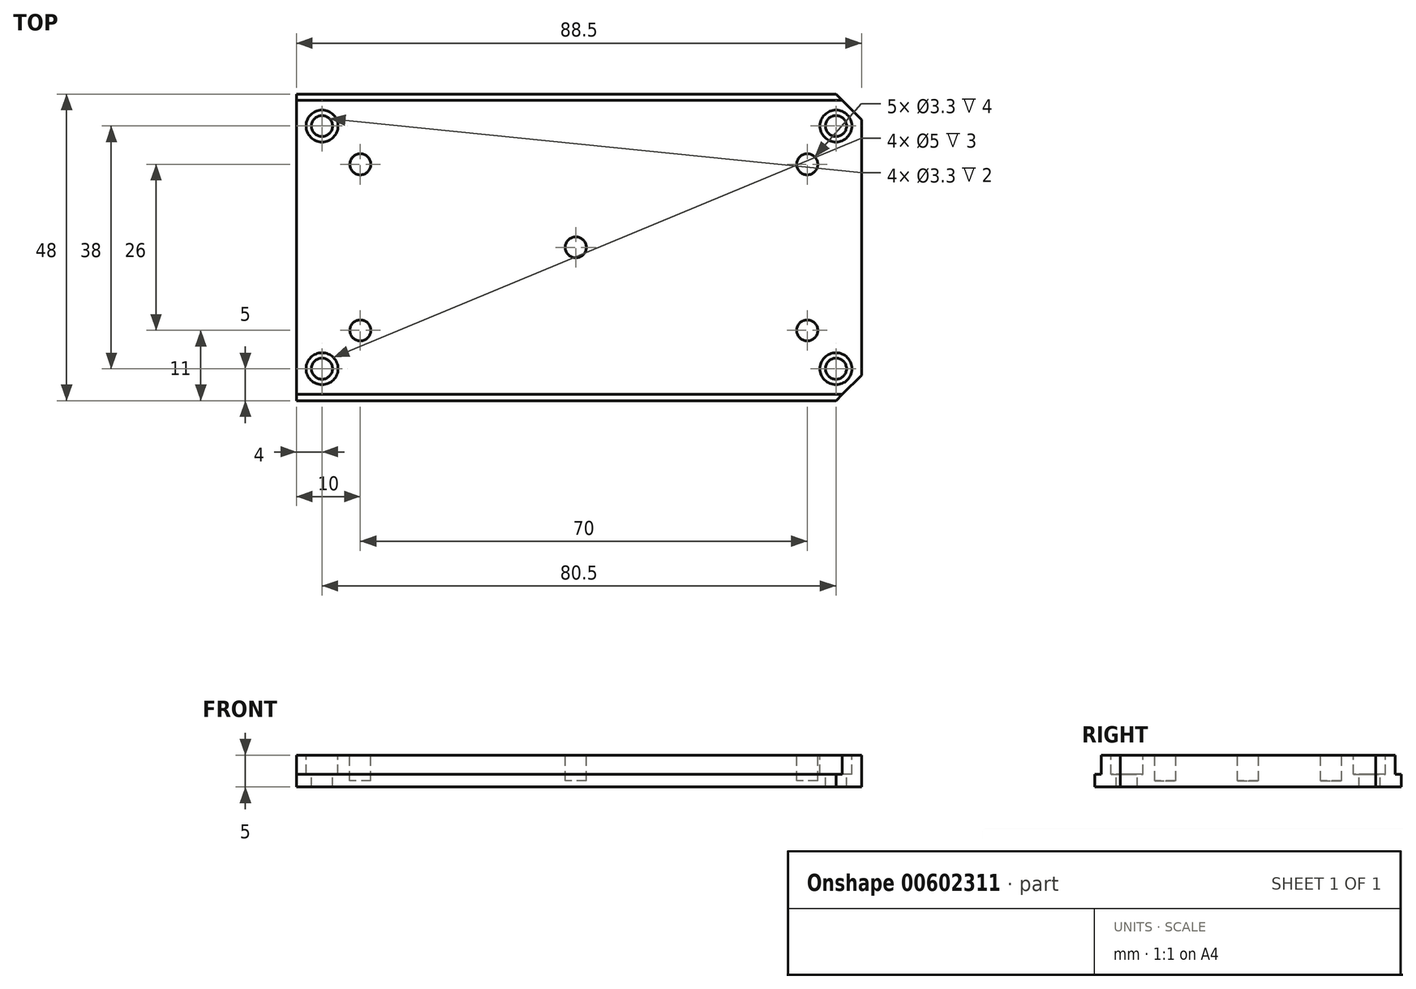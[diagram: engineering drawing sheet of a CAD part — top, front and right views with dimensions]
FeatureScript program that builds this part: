
annotation { "Feature Type Name" : "Feature", "Feature Type Description" : "" }
export const myFeature = defineFeature(function(context is Context, id is Id, definition is map)
    precondition{}
    {
        {
            var Q0;
            Q0=qCreatedBy(makeId("Top.planeOp"),FACE);
            var sketch = newSketch(context, id + "F0", { "sketchPlane" : qUnion([Q0])});
            skLineSegment(sketch, "E0.bottom", {"start": v(0, 0) * mm, "end": v(88.5, 0) * mm});
            skLineSegment(sketch, "E0.top", {"start": v(0, 46) * mm, "end": v(88.5, 46) * mm});
            skLineSegment(sketch, "E0.left", {"start": v(0, 0) * mm, "end": v(0, 46) * mm});
            skLineSegment(sketch, "E0.right", {"start": v(88.5, 0) * mm, "end": v(88.5, 46) * mm});
            skSolve(sketch);
        }
        {
            var Q0;
            Q0=makeQuery(id+"F0.imprint","IMPRINT",FACE,{"disambiguationData":[TD([[makeQuery(id+"F0.imprint","IMPRINT",EDGE,{"derivedFrom":sQuery(id+"F0.wireOp",EDGE,"E0.bottom")}),1.0]])]});
            extrude(context, id + "F1", {"entities" : qUnion([Q0]), "depth" : 5 * mm, "offsetDistance" : 25 * mm});
        }
        {
            var Q0;
            Q0=makeQuery(id+"F1.opExtrude","CAP_FACE",FACE,{"disambiguationData":[OSD([sQuery(id+"F0.wireOp",EDGE,"E0.bottom"),sQuery(id+"F0.wireOp",EDGE,"E0.top"),sQuery(id+"F0.wireOp",EDGE,"E0.left"),sQuery(id+"F0.wireOp",EDGE,"E0.right")])],"isStart":false});
            var sketch = newSketch(context, id + "F2", { "sketchPlane" : qUnion([Q0])});
            skCircle(sketch, "E1", {"center": v(4, 42) * mm, "radius": 2.5 * mm});
            skSolve(sketch);
        }
        {
            var Q0;
            Q0=makeQuery(id+"F2.imprint","IMPRINT",FACE,{"disambiguationData":[TD([[makeQuery(id+"F2.imprint","IMPRINT",EDGE,{"derivedFrom":sQuery(id+"F2.wireOp",EDGE,"E1")}),-1.0]])]});
            var sketch = newSketch(context, id + "F3", { "sketchPlane" : qUnion([Q0])});
            skCircle(sketch, "E2", {"center": v(4, 4) * mm, "radius": 2.5 * mm});
            skSolve(sketch);
        }
        {
            var Q0;
            Q0=makeQuery(id+"F2.imprint","IMPRINT",FACE,{"disambiguationData":[TD([[makeQuery(id+"F2.imprint","IMPRINT",EDGE,{"derivedFrom":sQuery(id+"F2.wireOp",EDGE,"E1")}),-1.0]])]});
            var sketch = newSketch(context, id + "F4", { "sketchPlane" : qUnion([Q0])});
            skCircle(sketch, "E3", {"center": v(84.5, 42) * mm, "radius": 2.5 * mm});
            skSolve(sketch);
        }
        {
            var Q0;
            Q0=makeQuery(id+"F2.imprint","IMPRINT",FACE,{"disambiguationData":[TD([[makeQuery(id+"F2.imprint","IMPRINT",EDGE,{"derivedFrom":sQuery(id+"F2.wireOp",EDGE,"E1")}),-1.0]])]});
            var sketch = newSketch(context, id + "F5", { "sketchPlane" : qUnion([Q0])});
            skCircle(sketch, "E4", {"center": v(84.5, 4) * mm, "radius": 2.5 * mm});
            skSolve(sketch);
        }
        {
            var Q0;
            Q0=makeQuery(id+"F2.imprint","IMPRINT",FACE,{"disambiguationData":[TD([[makeQuery(id+"F2.imprint","IMPRINT",EDGE,{"derivedFrom":sQuery(id+"F2.wireOp",EDGE,"E1")}),1.0]])]});
            extrude(context, id + "F6", {"entities" : qUnion([Q0]), "operationType" : NewBodyOperationType.REMOVE, "oppositeDirection" : true, "depth" : 3 * mm, "offsetDistance" : 25 * mm});
        }
        {
            var Q0;
            Q0=makeQuery(id+"F3.imprint","IMPRINT",FACE,{"disambiguationData":[TD([[makeQuery(id+"F3.imprint","IMPRINT",EDGE,{"derivedFrom":sQuery(id+"F3.wireOp",EDGE,"E2")}),1.0]])]});
            extrude(context, id + "F7", {"entities" : qUnion([Q0]), "operationType" : NewBodyOperationType.REMOVE, "oppositeDirection" : true, "depth" : 3 * mm, "offsetDistance" : 25 * mm});
        }
        {
            var Q0;
            Q0=makeQuery(id+"F4.imprint","IMPRINT",FACE,{"disambiguationData":[TD([[makeQuery(id+"F4.imprint","IMPRINT",EDGE,{"derivedFrom":sQuery(id+"F4.wireOp",EDGE,"E3")}),1.0]])]});
            extrude(context, id + "F8", {"entities" : qUnion([Q0]), "operationType" : NewBodyOperationType.REMOVE, "oppositeDirection" : true, "depth" : 3 * mm, "offsetDistance" : 25 * mm});
        }
        {
            var Q0;
            Q0=makeQuery(id+"F5.imprint","IMPRINT",FACE,{"disambiguationData":[TD([[makeQuery(id+"F5.imprint","IMPRINT",EDGE,{"derivedFrom":sQuery(id+"F5.wireOp",EDGE,"E4")}),1.0]])]});
            extrude(context, id + "F9", {"entities" : qUnion([Q0]), "operationType" : NewBodyOperationType.REMOVE, "oppositeDirection" : true, "depth" : 3 * mm, "offsetDistance" : 25 * mm});
        }
        {
            var Q0;
            Q0=makeQuery(id+"F6.boolean.opBoolean","COPY",FACE,{"derivedFrom":makeQuery(id+"F6.opExtrude","CAP_FACE",FACE,{"disambiguationData":[OSD([sQuery(id+"F2.wireOp",EDGE,"E1")])],"isStart":false})});
            var sketch = newSketch(context, id + "F10", { "sketchPlane" : qUnion([Q0])});
            skCircle(sketch, "E5", {"center": v(4, 42) * mm, "radius": 1.65 * mm});
            skSolve(sketch);
        }
        {
            var Q0;
            Q0=makeQuery(id+"F7.boolean.opBoolean","COPY",FACE,{"derivedFrom":makeQuery(id+"F7.opExtrude","CAP_FACE",FACE,{"disambiguationData":[OSD([sQuery(id+"F3.wireOp",EDGE,"E2")])],"isStart":false})});
            var sketch = newSketch(context, id + "F11", { "sketchPlane" : qUnion([Q0])});
            skCircle(sketch, "E6", {"center": v(4, 4) * mm, "radius": 1.65 * mm});
            skSolve(sketch);
        }
        {
            var Q0;
            Q0=makeQuery(id+"F8.boolean.opBoolean","COPY",FACE,{"derivedFrom":makeQuery(id+"F8.opExtrude","CAP_FACE",FACE,{"disambiguationData":[OSD([sQuery(id+"F4.wireOp",EDGE,"E3")])],"isStart":false})});
            var sketch = newSketch(context, id + "F12", { "sketchPlane" : qUnion([Q0])});
            skCircle(sketch, "E7", {"center": v(84.5, 42) * mm, "radius": 1.65 * mm});
            skSolve(sketch);
        }
        {
            var Q0;
            Q0=makeQuery(id+"F9.boolean.opBoolean","COPY",FACE,{"derivedFrom":makeQuery(id+"F9.opExtrude","CAP_FACE",FACE,{"disambiguationData":[OSD([sQuery(id+"F5.wireOp",EDGE,"E4")])],"isStart":false})});
            var sketch = newSketch(context, id + "F13", { "sketchPlane" : qUnion([Q0])});
            skCircle(sketch, "E8", {"center": v(84.5, 4) * mm, "radius": 1.65 * mm});
            skSolve(sketch);
        }
        {
            var Q0;
            Q0=makeQuery(id+"F12.imprint","IMPRINT",FACE,{"disambiguationData":[TD([[makeQuery(id+"F12.imprint","IMPRINT",EDGE,{"derivedFrom":sQuery(id+"F12.wireOp",EDGE,"E7")}),1.0]])]});
            extrude(context, id + "F14", {"entities" : qUnion([Q0]), "operationType" : NewBodyOperationType.REMOVE, "oppositeDirection" : true, "depth" : 3 * mm, "offsetDistance" : 25 * mm});
        }
        {
            var Q0;
            Q0=makeQuery(id+"F13.imprint","IMPRINT",FACE,{"disambiguationData":[TD([[makeQuery(id+"F13.imprint","IMPRINT",EDGE,{"derivedFrom":sQuery(id+"F13.wireOp",EDGE,"E8")}),1.0]])]});
            extrude(context, id + "F15", {"entities" : qUnion([Q0]), "operationType" : NewBodyOperationType.REMOVE, "oppositeDirection" : true, "depth" : 3 * mm, "offsetDistance" : 25 * mm});
        }
        {
            var Q0;
            Q0=makeQuery(id+"F11.imprint","IMPRINT",FACE,{"disambiguationData":[TD([[makeQuery(id+"F11.imprint","IMPRINT",EDGE,{"derivedFrom":sQuery(id+"F11.wireOp",EDGE,"E6")}),1.0]])]});
            extrude(context, id + "F16", {"entities" : qUnion([Q0]), "operationType" : NewBodyOperationType.REMOVE, "oppositeDirection" : true, "depth" : 3 * mm, "offsetDistance" : 25 * mm});
        }
        {
            var Q0;
            Q0=makeQuery(id+"F10.imprint","IMPRINT",FACE,{"disambiguationData":[TD([[makeQuery(id+"F10.imprint","IMPRINT",EDGE,{"derivedFrom":sQuery(id+"F10.wireOp",EDGE,"E5")}),1.0]])]});
            extrude(context, id + "F17", {"entities" : qUnion([Q0]), "operationType" : NewBodyOperationType.REMOVE, "oppositeDirection" : true, "depth" : 3 * mm, "offsetDistance" : 25 * mm});
        }
        {
            var Q0;
            Q0=makeQuery(id+"F1.opExtrude","CAP_FACE",FACE,{"disambiguationData":[OSD([sQuery(id+"F0.wireOp",EDGE,"E0.bottom"),sQuery(id+"F0.wireOp",EDGE,"E0.top"),sQuery(id+"F0.wireOp",EDGE,"E0.left"),sQuery(id+"F0.wireOp",EDGE,"E0.right")])],"isStart":false});
            var sketch = newSketch(context, id + "F18", { "sketchPlane" : qUnion([Q0])});
            skCircle(sketch, "E9", {"center": v(43.75, 23) * mm, "radius": 1.65 * mm});
            skSolve(sketch);
        }
        {
            var Q0;
            Q0=makeQuery(id+"F18.imprint","IMPRINT",FACE,{"disambiguationData":[TD([[makeQuery(id+"F18.imprint","IMPRINT",EDGE,{"derivedFrom":sQuery(id+"F18.wireOp",EDGE,"E9")}),1.0]])]});
            extrude(context, id + "F19", {"entities" : qUnion([Q0]), "operationType" : NewBodyOperationType.REMOVE, "oppositeDirection" : true, "depth" : 4 * mm, "offsetDistance" : 25 * mm});
        }
        {
            var Q0;
            Q0=makeQuery(id+"F1.opExtrude","CAP_FACE",FACE,{"disambiguationData":[OSD([sQuery(id+"F0.wireOp",EDGE,"E0.bottom"),sQuery(id+"F0.wireOp",EDGE,"E0.top"),sQuery(id+"F0.wireOp",EDGE,"E0.left"),sQuery(id+"F0.wireOp",EDGE,"E0.right")])],"isStart":false});
            var sketch = newSketch(context, id + "F20", { "sketchPlane" : qUnion([Q0])});
            skCircle(sketch, "E10", {"center": v(10, 36) * mm, "radius": 1.65 * mm});
            skSolve(sketch);
        }
        {
            var Q0;
            Q0=makeQuery(id+"F20.imprint","IMPRINT",FACE,{"disambiguationData":[TD([[makeQuery(id+"F20.imprint","IMPRINT",EDGE,{"derivedFrom":sQuery(id+"F20.wireOp",EDGE,"E10")}),-1.0]])]});
            var sketch = newSketch(context, id + "F21", { "sketchPlane" : qUnion([Q0])});
            skCircle(sketch, "E11", {"center": v(10, 10) * mm, "radius": 1.65 * mm});
            skSolve(sketch);
        }
        {
            var Q0;
            Q0=makeQuery(id+"F20.imprint","IMPRINT",FACE,{"disambiguationData":[TD([[makeQuery(id+"F20.imprint","IMPRINT",EDGE,{"derivedFrom":sQuery(id+"F20.wireOp",EDGE,"E10")}),-1.0]])]});
            var sketch = newSketch(context, id + "F22", { "sketchPlane" : qUnion([Q0])});
            skCircle(sketch, "E12", {"center": v(80, 36) * mm, "radius": 1.65 * mm});
            skSolve(sketch);
        }
        {
            var Q0;
            Q0=makeQuery(id+"F20.imprint","IMPRINT",FACE,{"disambiguationData":[TD([[makeQuery(id+"F20.imprint","IMPRINT",EDGE,{"derivedFrom":sQuery(id+"F20.wireOp",EDGE,"E10")}),-1.0]])]});
            var sketch = newSketch(context, id + "F23", { "sketchPlane" : qUnion([Q0])});
            skCircle(sketch, "E13", {"center": v(80, 10) * mm, "radius": 1.65 * mm});
            skSolve(sketch);
        }
        {
            var Q0;
            Q0=makeQuery(id+"F20.imprint","IMPRINT",FACE,{"disambiguationData":[TD([[makeQuery(id+"F20.imprint","IMPRINT",EDGE,{"derivedFrom":sQuery(id+"F20.wireOp",EDGE,"E10")}),1.0]])]});
            var Q1;
            Q1=makeQuery(id+"F21.imprint","IMPRINT",FACE,{"disambiguationData":[TD([[makeQuery(id+"F21.imprint","IMPRINT",EDGE,{"derivedFrom":sQuery(id+"F21.wireOp",EDGE,"E11")}),1.0]])]});
            extrude(context, id + "F24", {"entities" : qUnion([Q0, Q1]), "operationType" : NewBodyOperationType.REMOVE, "oppositeDirection" : true, "depth" : 4 * mm, "offsetDistance" : 25 * mm});
        }
        {
            var Q0;
            Q0=makeQuery(id+"F22.imprint","IMPRINT",FACE,{"disambiguationData":[TD([[makeQuery(id+"F22.imprint","IMPRINT",EDGE,{"derivedFrom":sQuery(id+"F22.wireOp",EDGE,"E12")}),1.0]])]});
            var Q1;
            Q1=makeQuery(id+"F23.imprint","IMPRINT",FACE,{"disambiguationData":[TD([[makeQuery(id+"F23.imprint","IMPRINT",EDGE,{"derivedFrom":sQuery(id+"F23.wireOp",EDGE,"E13")}),1.0]])]});
            extrude(context, id + "F25", {"entities" : qUnion([Q0, Q1]), "operationType" : NewBodyOperationType.REMOVE, "oppositeDirection" : true, "depth" : 4 * mm, "offsetDistance" : 25 * mm});
        }
        {
            var Q0;
            Q0=makeQuery(id+"F1.opExtrude","SWEPT_FACE",FACE,{"disambiguationData":[OSD([sQuery(id+"F0.wireOp",EDGE,"E0.top")])]});
            var sketch = newSketch(context, id + "F26", { "sketchPlane" : qUnion([Q0])});
            skLineSegment(sketch, "E14.bottom", {"start": v(-88.5, 2) * mm, "end": v(0, 2) * mm});
            skLineSegment(sketch, "E14.top", {"start": v(-88.5, 0) * mm, "end": v(0, 0) * mm});
            skLineSegment(sketch, "E14.left", {"start": v(-88.5, 2) * mm, "end": v(-88.5, 0) * mm});
            skLineSegment(sketch, "E14.right", {"start": v(0, 2) * mm, "end": v(0, 0) * mm});
            skSolve(sketch);
        }
        {
            var Q0;
            Q0=makeQuery(id+"F26.imprint","IMPRINT",FACE,{"disambiguationData":[TD([[makeQuery(id+"F26.imprint","IMPRINT",EDGE,{"derivedFrom":sQuery(id+"F26.wireOp",EDGE,"E14.bottom")}),-1.0]])]});
            extrude(context, id + "F27", {"entities" : qUnion([Q0]), "operationType" : NewBodyOperationType.ADD, "depth" : 1 * mm, "offsetDistance" : 25 * mm});
        }
        {
            var Q0;
            Q0=makeQuery(id+"F1.opExtrude","SWEPT_FACE",FACE,{"disambiguationData":[OSD([sQuery(id+"F0.wireOp",EDGE,"E0.bottom")])]});
            var sketch = newSketch(context, id + "F28", { "sketchPlane" : qUnion([Q0])});
            skLineSegment(sketch, "E15.bottom", {"start": v(0, 2) * mm, "end": v(88.5, 2) * mm});
            skLineSegment(sketch, "E15.top", {"start": v(0, 0) * mm, "end": v(88.5, 0) * mm});
            skLineSegment(sketch, "E15.left", {"start": v(0, 2) * mm, "end": v(0, 0) * mm});
            skLineSegment(sketch, "E15.right", {"start": v(88.5, 2) * mm, "end": v(88.5, 0) * mm});
            skSolve(sketch);
        }
        {
            var Q0;
            Q0=makeQuery(id+"F28.imprint","IMPRINT",FACE,{"disambiguationData":[TD([[makeQuery(id+"F28.imprint","IMPRINT",EDGE,{"derivedFrom":sQuery(id+"F28.wireOp",EDGE,"E15.bottom")}),-1.0]])]});
            extrude(context, id + "F29", {"entities" : qUnion([Q0]), "operationType" : NewBodyOperationType.ADD, "depth" : 1 * mm, "offsetDistance" : 25 * mm});
        }
        {
            var Q0;
            Q0=makeQuery(id+"F1.opExtrude","SWEPT_EDGE",EDGE,{"disambiguationData":[OSD([sQuery(id+"F0.wireOp",EDGE,"E0.bottom"),sQuery(id+"F0.wireOp",EDGE,"E0.right")])]});
            chamfer(context, id + "F30", {"entities" : qUnion([Q0]), "width" : 3 * mm, "tangentPropagation" : true});
        }
        {
            var Q0;
            Q0=makeQuery(id+"F29.opExtrude","SWEPT_FACE",FACE,{"disambiguationData":[OSD([sQuery(id+"F28.wireOp",EDGE,"E15.bottom")])]});
            var sketch = newSketch(context, id + "F31", { "sketchPlane" : qUnion([Q0])});
            skLineSegment(sketch, "E16", {"start": v(88.5, 3) * mm, "end": v(84.5, -1) * mm});
            skLineSegment(sketch, "E17", {"start": v(84.5, -1) * mm, "end": v(88.5, -1) * mm});
            skLineSegment(sketch, "E18", {"start": v(88.5, -1) * mm, "end": v(88.5, 3) * mm});
            skSolve(sketch);
        }
        {
            var Q0;
            {var subQ4=sQuery(id+"F31.wireOp",EDGE,"E17");Q0=makeQuery(id+"F31.imprint","IMPRINT",FACE,{"disambiguationData":[TD([[makeQuery(id+"F31.imprint","IMPRINT",EDGE,{"derivedFrom":subQ4}),1.0]])]});}
            extrude(context, id + "F32", {"entities" : qUnion([Q0]), "operationType" : NewBodyOperationType.REMOVE, "oppositeDirection" : true, "depth" : 3 * mm, "offsetDistance" : 25 * mm});
        }
        {
            var Q0;
            Q0=makeQuery(id+"F1.opExtrude","SWEPT_EDGE",EDGE,{"disambiguationData":[OSD([sQuery(id+"F0.wireOp",EDGE,"E0.top"),sQuery(id+"F0.wireOp",EDGE,"E0.right")])]});
            chamfer(context, id + "F33", {"entities" : qUnion([Q0]), "width" : 3 * mm, "tangentPropagation" : true});
        }
        {
            var Q0;
            Q0=makeQuery(id+"F27.opExtrude","SWEPT_FACE",FACE,{"disambiguationData":[OSD([sQuery(id+"F26.wireOp",EDGE,"E14.bottom")])]});
            var sketch = newSketch(context, id + "F34", { "sketchPlane" : qUnion([Q0])});
            skLineSegment(sketch, "E19", {"start": v(88.5, 43) * mm, "end": v(84.5, 47) * mm});
            skLineSegment(sketch, "E20", {"start": v(84.5, 47) * mm, "end": v(88.5, 47) * mm});
            skLineSegment(sketch, "E21", {"start": v(88.5, 47) * mm, "end": v(88.5, 43) * mm});
            skSolve(sketch);
        }
        {
            var Q0;
            {var subQ4=sQuery(id+"F34.wireOp",EDGE,"E20");Q0=makeQuery(id+"F34.imprint","IMPRINT",FACE,{"disambiguationData":[TD([[makeQuery(id+"F34.imprint","IMPRINT",EDGE,{"derivedFrom":subQ4}),1.0]])]});}
            extrude(context, id + "F35", {"entities" : qUnion([Q0]), "operationType" : NewBodyOperationType.REMOVE, "oppositeDirection" : true, "depth" : 3 * mm, "offsetDistance" : 25 * mm});
        }
    });
